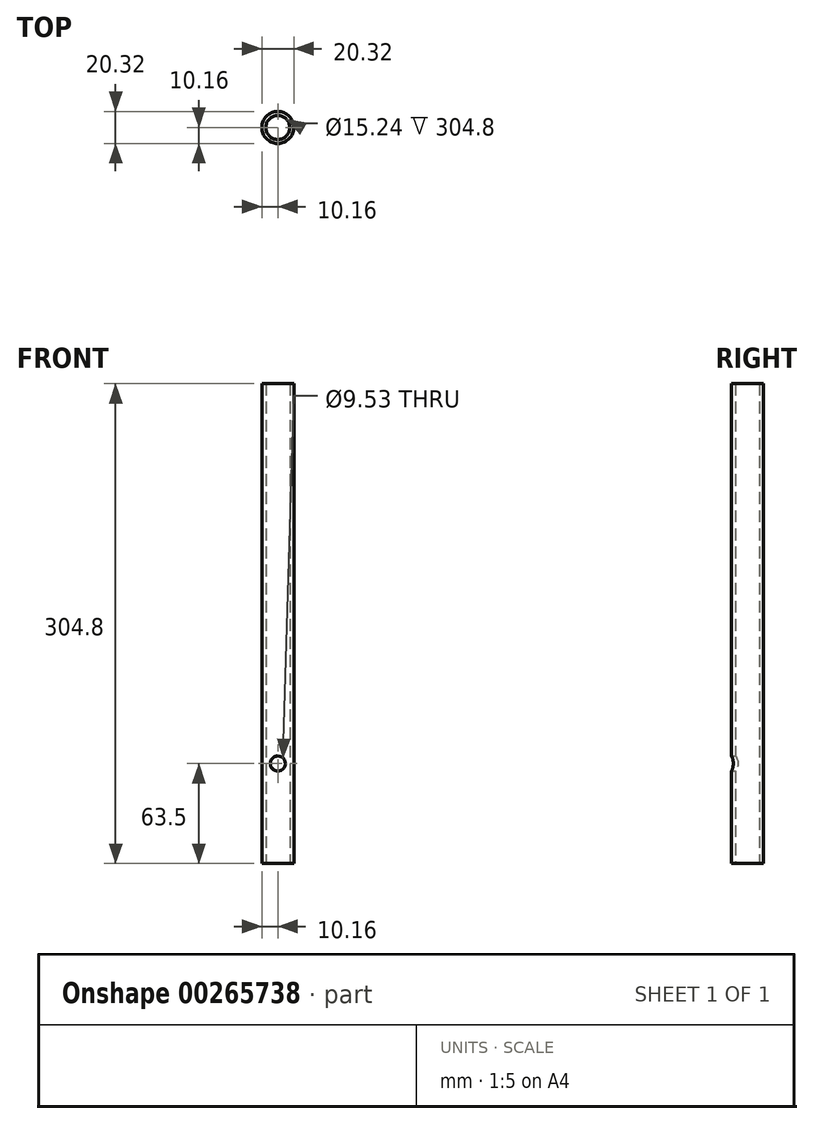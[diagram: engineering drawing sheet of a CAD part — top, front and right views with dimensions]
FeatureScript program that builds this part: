
annotation { "Feature Type Name" : "Feature", "Feature Type Description" : "" }
export const myFeature = defineFeature(function(context is Context, id is Id, definition is map)
    precondition{}
    {
        {
            var Q0;
            Q0=qCreatedBy(makeId("Top.planeOp"),FACE);
            var sketch = newSketch(context, id + "F0", { "sketchPlane" : qUnion([Q0])});
            skCircle(sketch, "E0", {"center": v(0, 0) * mm, "radius": 10.16 * mm});
            skCircle(sketch, "E1", {"center": v(0, 0) * mm, "radius": 7.62 * mm});
            skSolve(sketch);
        }
        {
            var Q0;
            Q0=qSketchRegion(id+"F0",true);
            extrude(context, id + "F1", {"entities" : qUnion([Q0]), "depth" : 304.8 * mm});
        }
        {
            var Q0;
            Q0=qCreatedBy(makeId("Front.planeOp"),FACE);
            var sketch = newSketch(context, id + "F2", { "sketchPlane" : qUnion([Q0])});
            skCircle(sketch, "E2", {"center": v(0, 63.5) * mm, "radius": 4.76 * mm});
            skSolve(sketch);
        }
        {
            var Q0;
            Q0=qSketchRegion(id+"F2",true);
            extrude(context, id + "F3", {"entities" : qUnion([Q0]), "operationType" : NewBodyOperationType.REMOVE, "endBound" : BoundingType.THROUGH_ALL, "depth" : 25.4 * mm});
        }
    });
